# Revit family: Reece_Toilet_American Standard_Signature_Back to Wall_Rimless
name_source: partatom
category: Plumbing Fixtures
revit_build: Autodesk Revit 2018 (Build: 20180329_1100(x64)
units: mm (PartAtom-declared; Revit-internal decimal feet)

## family parameters
Always vertical = Yes
Cut with Voids When Loaded = No
Part Type = Normal
Room Calculation Point = No
Round Connector Dimension = Use Diameter
Shared = No
Work Plane-Based = No

## types (1)
- Soft Close_Vitreous China_White
    Description = American Standard Signature Hygiene Rim Back to Wall Pan with Soft Close Quick Release White Seat (4 Star)
    Disclaimer = THIS FILE IS THE PROPERTY OF THE REECE GROUP. IT MAY NOT BE REPRODUCED, REVERSE-ENGINEERED OR MODIFIED. ANY REPUBLICATION, TRANSMISSION OR DISTRIBUTION FOR THE PURPOSE OF COMMERCIALLY EXPLOITING THE FILES IS PROHIBITED.
    Keynote = Product #9509680, Reece_Toilet_American Standard_Signature_Back to Wall_Rimless - Soft Close_Vitreous China_White
    Manufacturer = American Standard
    Model = Signature
    Reece_Back_Inlet = 45 mm  [stored 0.147638 ft]
    Reece_Back_Outlet_Offset = 180 mm  [stored 0.590551 ft]
    Reece_Bottom_Outlet_Offset = 90 mm  [stored 0.295276 ft]
    Reece_Detail_Additional = Back to Wall
    Reece_Detail_Disclaimer = THIS FILE IS THE PROPERTY OF THE REECE GROUP. IT MAY NOT BE REPRODUCED, REVERSE-ENGINEERED OR MODIFIED. ANY REPUBLICATION, TRANSMISSION OR DISTRIBUTION FOR THE PURPOSE OF COMMERCIALLY EXPLOITING THE FILES IS PROHIBITED.
    Reece_Detail_Function = Universal S & P
    Reece_Detail_Shape = Rimless
    Reece_Material_Colour = Reece_Plastic_CrystaSleek_White
    Reece_Material_Main = Reece_Vitreous China_White
    Reece_Material_Seat = Reece_Plastic_CrystaSleek_White
    Reece_Material_Secondary = Reece_Brass_Chrome
    Reece_Overall_Height = 430 mm
    Reece_Overall_Projection = 560 mm  [stored 1.83727 ft]
    Reece_Overall_Width = 382 mm  [stored 1.25328 ft]
    Reece_P_Trap = 102 mm
    Reece_Pan_Height = 400 mm  [stored 1.31234 ft]
    Reece_Product_Brand = American Standard
    Reece_Product_Description = American Standard Signature Hygiene Rim Back to Wall Pan CrystaSleek with Soft Close Quick Release White Seat (4 Star)
    Reece_Product_Mount = Floor Mounted
    Reece_Product_Number = 9509680
    Reece_Product_Sub Brand = Signature
    Reece_Product_Type = Toilet
    Reece_Product_Web Page = https://www.reece.com.au
    Reece_S_Trap = 102 mm
    Type Comments = Toilet
    URL = https://www.reece.com.au

note: [stored X ft] marks values corroborated as IEEE doubles in the binary element streams (Revit-internal decimal feet)

## geometry (parser evidence)
native form markers: Sweep x6
no freeform markers — native parametric forms only
